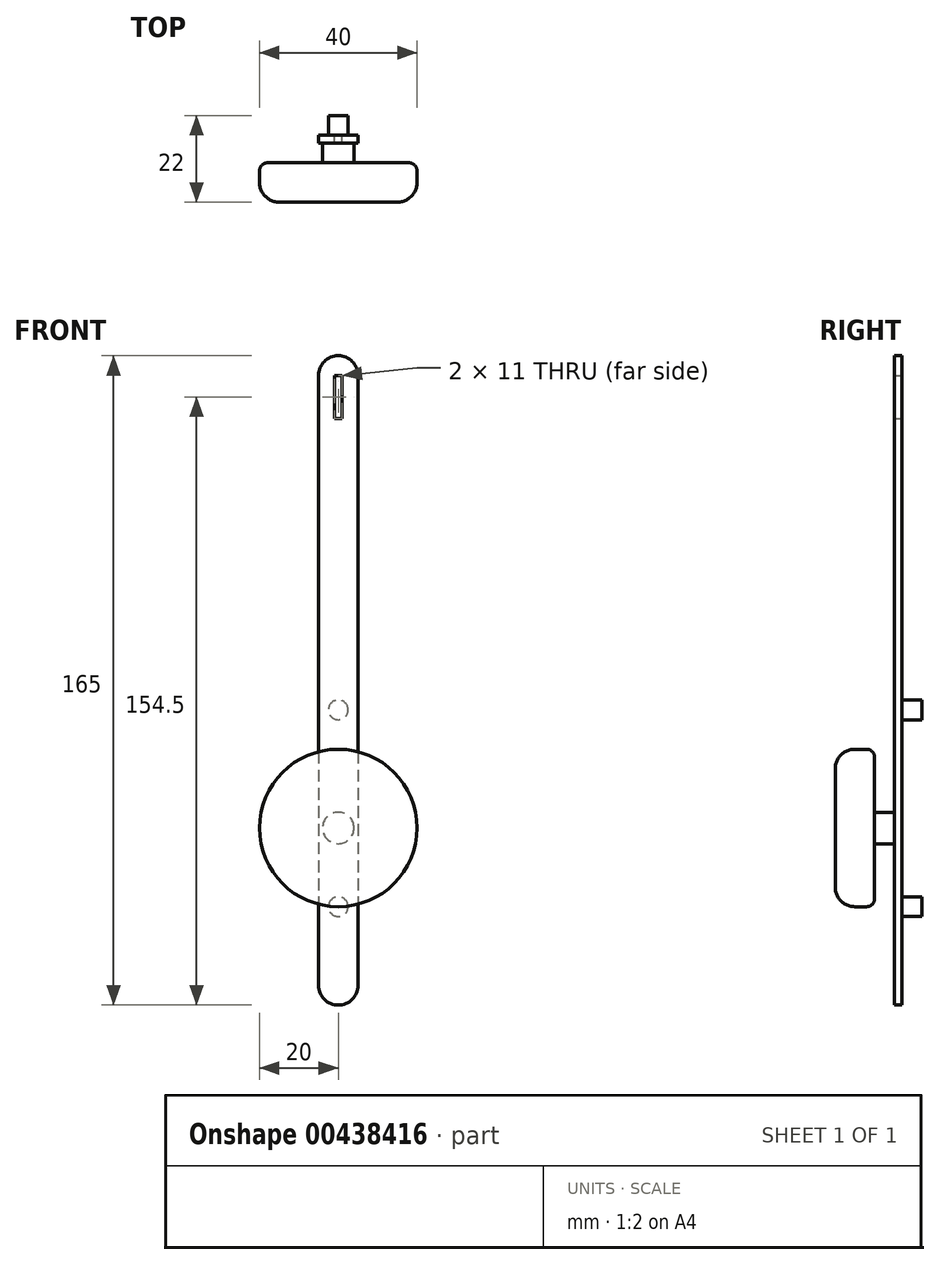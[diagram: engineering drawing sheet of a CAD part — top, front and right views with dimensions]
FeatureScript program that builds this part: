
annotation { "Feature Type Name" : "Feature", "Feature Type Description" : "" }
export const myFeature = defineFeature(function(context is Context, id is Id, definition is map)
    precondition{}
    {
        {
            var Q0;
            Q0=qCreatedBy(makeId("Front.planeOp"),FACE);
            var sketch = newSketch(context, id + "F0", { "sketchPlane" : qUnion([Q0])});
            skLineSegment(sketch, "E0.bottom", {"start": v(0, 82.5) * mm, "end": v(0, 82.5) * mm});
            skLineSegment(sketch, "E0.top", {"start": v(0, -82.5) * mm, "end": v(0, -82.5) * mm});
            skLineSegment(sketch, "E0.left", {"start": v(5, 77.5) * mm, "end": v(5, -77.5) * mm});
            skLineSegment(sketch, "E0.right", {"start": v(-5, 77.5) * mm, "end": v(-5, -77.5) * mm});
            skPoint(sketch, "E0.middle", {"position": v(0, 0) * mm});
            skCircle(sketch, "E1", {"center": v(0, -7.5) * mm, "radius": 2.5 * mm});
            skCircle(sketch, "E2", {"center": v(0, -17.5) * mm, "radius": 2.5 * mm});
            skCircle(sketch, "E3", {"center": v(0, -57.5) * mm, "radius": 2.5 * mm});
            skCircle(sketch, "E4", {"center": v(0, -67.5) * mm, "radius": 2.5 * mm});
            skLineSegment(sketch, "E5.bottom", {"start": v(1, 66.5) * mm, "end": v(-1, 66.5) * mm});
            skLineSegment(sketch, "E5.top", {"start": v(1, 77.5) * mm, "end": v(-1, 77.5) * mm});
            skLineSegment(sketch, "E5.left", {"start": v(1, 66.5) * mm, "end": v(1, 77.5) * mm});
            skLineSegment(sketch, "E5.right", {"start": v(-1, 66.5) * mm, "end": v(-1, 77.5) * mm});
            skPoint(sketch, "E5.middle", {"position": v(0, 72) * mm});
            skPoint(sketch, "E6.visualSharp", {"position": v(-5, 82.5) * mm});
            skArc(sketch, "E6.filletArc", {"start": v(0, 82.5) * mm, "mid": v(-3.54, 81.04) * mm, "end": v(-5, 77.5) * mm});
            skPoint(sketch, "E7.visualSharp", {"position": v(5, 82.5) * mm});
            skArc(sketch, "E7.filletArc", {"start": v(5, 77.5) * mm, "mid": v(3.54, 81.04) * mm, "end": v(0, 82.5) * mm});
            skPoint(sketch, "E8.visualSharp", {"position": v(5, -82.5) * mm});
            skArc(sketch, "E8.filletArc", {"start": v(0, -82.5) * mm, "mid": v(3.54, -81.04) * mm, "end": v(5, -77.5) * mm});
            skPoint(sketch, "E9.visualSharp", {"position": v(-5, -82.5) * mm});
            skArc(sketch, "E9.filletArc", {"start": v(-5, -77.5) * mm, "mid": v(-3.54, -81.04) * mm, "end": v(0, -82.5) * mm});
            skSolve(sketch);
        }
        {
            var Q0;
            Q0=makeQuery(id+"F0.imprint","IMPRINT",FACE,{"disambiguationData":[TD([[makeQuery(id+"F0.imprint","IMPRINT",EDGE,{"derivedFrom":sQuery(id+"F0.wireOp",EDGE,"E0.left")}),-1.0]])]});
            var Q1;
            Q1=makeQuery(id+"F0.imprint","IMPRINT",FACE,{"disambiguationData":[TD([[makeQuery(id+"F0.imprint","IMPRINT",EDGE,{"derivedFrom":sQuery(id+"F0.wireOp",EDGE,"E1")}),1.0]])]});
            var Q2;
            Q2=makeQuery(id+"F0.imprint","IMPRINT",FACE,{"disambiguationData":[TD([[makeQuery(id+"F0.imprint","IMPRINT",EDGE,{"derivedFrom":sQuery(id+"F0.wireOp",EDGE,"E2")}),1.0]])]});
            var Q3;
            Q3=makeQuery(id+"F0.imprint","IMPRINT",FACE,{"disambiguationData":[TD([[makeQuery(id+"F0.imprint","IMPRINT",EDGE,{"derivedFrom":sQuery(id+"F0.wireOp",EDGE,"E3")}),1.0]])]});
            var Q4;
            Q4=makeQuery(id+"F0.imprint","IMPRINT",FACE,{"disambiguationData":[TD([[makeQuery(id+"F0.imprint","IMPRINT",EDGE,{"derivedFrom":sQuery(id+"F0.wireOp",EDGE,"E4")}),1.0]])]});
            extrude(context, id + "F1", {"entities" : qUnion([Q0, Q1, Q2, Q3, Q4]), "depth" : 2 * mm});
        }
        {
            var Q0;
            Q0=makeQuery(id+"F0.imprint","IMPRINT",FACE,{"disambiguationData":[TD([[makeQuery(id+"F0.imprint","IMPRINT",EDGE,{"derivedFrom":sQuery(id+"F0.wireOp",EDGE,"E1")}),1.0]])]});
            var Q1;
            Q1=makeQuery(id+"F0.imprint","IMPRINT",FACE,{"disambiguationData":[TD([[makeQuery(id+"F0.imprint","IMPRINT",EDGE,{"derivedFrom":sQuery(id+"F0.wireOp",EDGE,"E3")}),1.0]])]});
            extrude(context, id + "F2", {"entities" : qUnion([Q0, Q1]), "operationType" : NewBodyOperationType.ADD, "oppositeDirection" : true, "depth" : 5 * mm});
        }
        {
            var Q0;
            Q0=makeQuery(id+"F1.opExtrude","CAP_FACE",FACE,{"disambiguationData":[OSD([sQuery(id+"F0.wireOp",EDGE,"E0.left"),sQuery(id+"F0.wireOp",EDGE,"E0.right"),sQuery(id+"F0.wireOp",EDGE,"E5.bottom"),sQuery(id+"F0.wireOp",EDGE,"E5.top"),sQuery(id+"F0.wireOp",EDGE,"E5.left"),sQuery(id+"F0.wireOp",EDGE,"E5.right"),sQuery(id+"F0.wireOp",EDGE,"E6.filletArc"),sQuery(id+"F0.wireOp",EDGE,"E7.filletArc"),sQuery(id+"F0.wireOp",EDGE,"E8.filletArc"),sQuery(id+"F0.wireOp",EDGE,"E9.filletArc")])],"isStart":false});
            var sketch = newSketch(context, id + "F3", { "sketchPlane" : qUnion([Q0])});
            skCircle(sketch, "E10.0", {"center": v(0, -17.5) * mm, "radius": 2.5 * mm, "construction": true});
            skCircle(sketch, "E10.1", {"center": v(0, -57.5) * mm, "radius": 2.5 * mm, "construction": true});
            skCircle(sketch, "E11", {"center": v(0, -37.5) * mm, "radius": 10 * mm});
            skCircle(sketch, "E12", {"center": v(0, -37.5) * mm, "radius": 4 * mm});
            skSolve(sketch);
        }
        {
            var Q0;
            Q0=makeQuery(id+"F3.imprint","IMPRINT",FACE,{"disambiguationData":[TD([[makeQuery(id+"F3.imprint","IMPRINT",EDGE,{"derivedFrom":sQuery(id+"F3.wireOp",EDGE,"E12")}),1.0]])]});
            extrude(context, id + "F4", {"entities" : qUnion([Q0]), "operationType" : NewBodyOperationType.ADD, "depth" : 5 * mm});
        }
        {
            var Q0;
            Q0=makeQuery(id+"F4.opExtrude","CAP_FACE",FACE,{"disambiguationData":[OSD([sQuery(id+"F3.wireOp",EDGE,"E12")])],"isStart":false});
            var sketch = newSketch(context, id + "F5", { "sketchPlane" : qUnion([Q0])});
            skCircle(sketch, "E13", {"center": v(0, -37.5) * mm, "radius": 20 * mm});
            skSolve(sketch);
        }
        {
            var Q0;
            Q0=makeQuery(id+"F5.imprint","IMPRINT",FACE,{"disambiguationData":[TD([[makeQuery(id+"F5.imprint","IMPRINT",EDGE,{"derivedFrom":sQuery(id+"F5.wireOp",EDGE,"E13")}),1.0]])]});
            var Q1;
            Q1=makeQuery(id+"F5.imprint","IMPRINT",FACE,{"disambiguationData":[TD([[makeQuery(id+"F5.imprint","IMPRINT",EDGE,{"derivedFrom":makeQuery(id+"F4.opExtrude","CAP_EDGE",EDGE,{"disambiguationData":[OSD([sQuery(id+"F3.wireOp",EDGE,"E12")])],"isStart":false})}),1.0]])]});
            extrude(context, id + "F6", {"entities" : qUnion([Q0, Q1]), "operationType" : NewBodyOperationType.ADD, "depth" : 10 * mm});
        }
        {
            var Q0;
            Q0=makeQuery(id+"F6.opExtrude","CAP_EDGE",EDGE,{"disambiguationData":[OSD([sQuery(id+"F5.wireOp",EDGE,"E13")])],"isStart":false});
            fillet(context, id + "F7", {"entities" : qUnion([Q0]), "radius" : 5 * mm, "tangentPropagation" : true, "allowEdgeOverflow" : false});
        }
        {
            var Q0;
            Q0=makeQuery(id+"F4.opExtrude","CAP_EDGE",EDGE,{"disambiguationData":[OSD([sQuery(id+"F3.wireOp",EDGE,"E12")])],"isStart":false});
            var Q1;
            Q1=makeQuery(id+"F6.opExtrude","CAP_EDGE",EDGE,{"disambiguationData":[OSD([sQuery(id+"F5.wireOp",EDGE,"E13")])],"isStart":true});
            fillet(context, id + "F8", {"entities" : qUnion([Q0, Q1]), "radius" : 2 * mm, "tangentPropagation" : true, "allowEdgeOverflow" : false});
        }
    });
